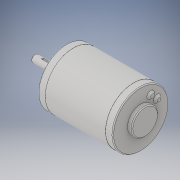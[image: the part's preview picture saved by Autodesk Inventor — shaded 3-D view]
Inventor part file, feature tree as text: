
AUTODESK INVENTOR PART (.ipt)
format: ipt  version: 2018 (Build 220112000, 112)  size: 170,496 bytes
history: native  units: in
note: dims shown in document units (in); Inventor stores cm internally (conversion verified against a paired STEP export)
features: chamfer x1
ambient origin geometry x8: Origin, YZ Plane, XZ Plane, XY Plane, X Axis, Y Axis, Z Axis, Center Point
bodies: Solid1 (feature_tree)
feature tree (1):
  chamfer  "Chamfer3"  [1 undecoded]
note: 1 required parameter value undecoded (feature->parameter linkage not recoverable at this tier; creation-order binding heuristic only, values carry confidence <= 0.55)
